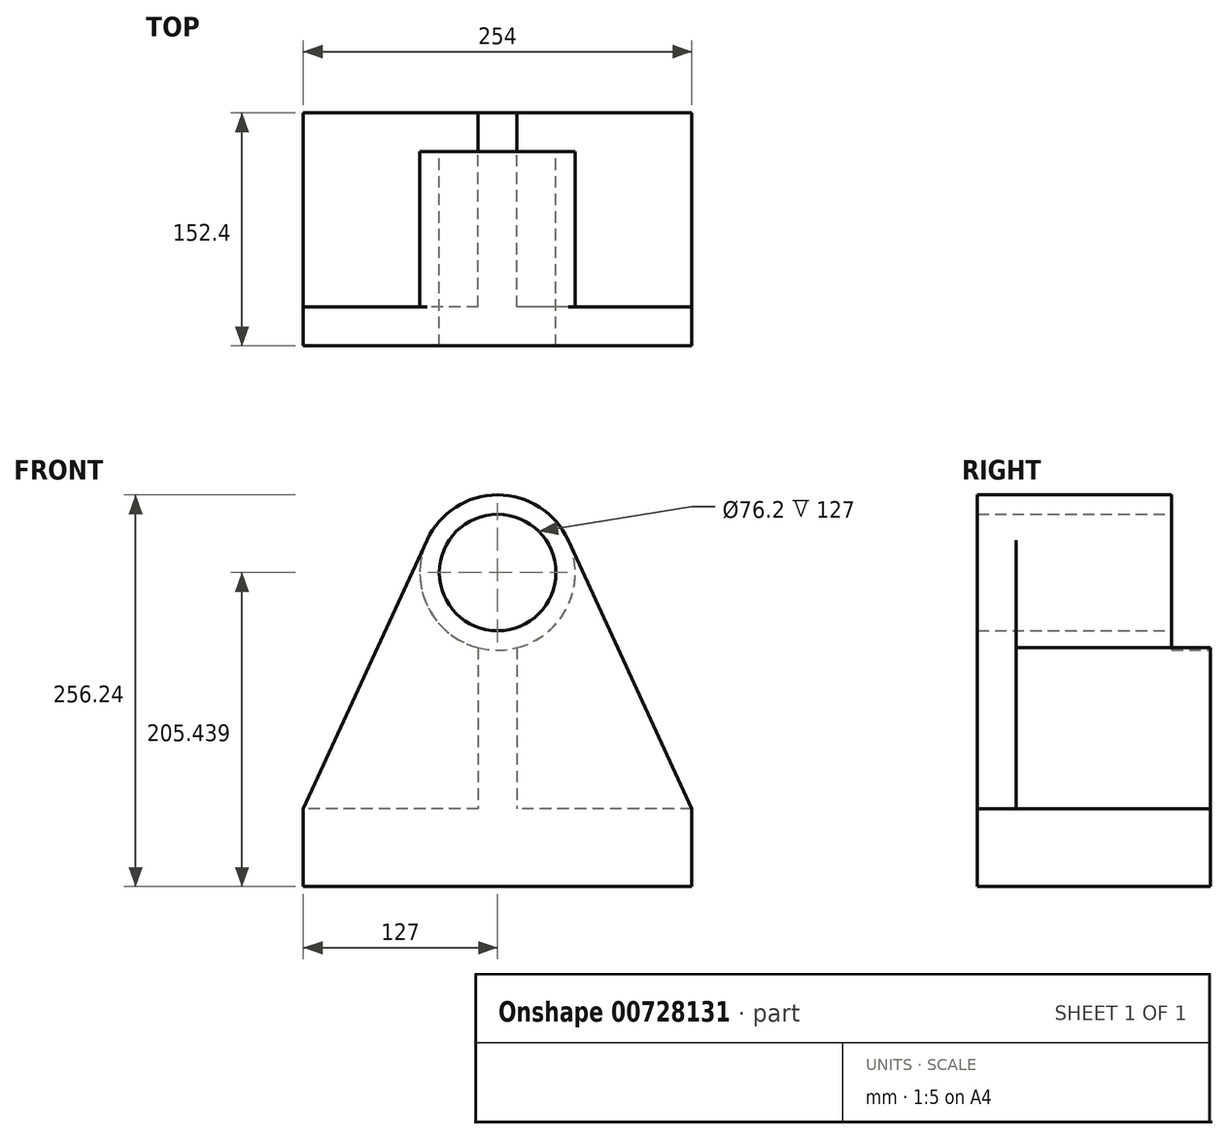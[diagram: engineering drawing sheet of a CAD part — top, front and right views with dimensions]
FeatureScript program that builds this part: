
annotation { "Feature Type Name" : "Feature", "Feature Type Description" : "" }
export const myFeature = defineFeature(function(context is Context, id is Id, definition is map)
    precondition{}
    {
        {
            var Q0;
            Q0=qCreatedBy(makeId("Front.planeOp"),FACE);
            var sketch = newSketch(context, id + "F0", { "sketchPlane" : qUnion([Q0])});
            skLineSegment(sketch, "E0", {"start": v(0, 0) * mm, "end": v(254, 0) * mm});
            skLineSegment(sketch, "E1", {"start": v(254, 0) * mm, "end": v(254, 50.8) * mm});
            skLineSegment(sketch, "E2", {"start": v(0, 0) * mm, "end": v(0, 50.8) * mm});
            skLineSegment(sketch, "E3", {"start": v(127, 0) * mm, "end": v(127, 205.44) * mm});
            skCircle(sketch, "E4", {"center": v(127, 205.44) * mm, "radius": 50.8 * mm});
            skLineSegment(sketch, "E5", {"start": v(254, 50.8) * mm, "end": v(173.16, 226.66) * mm});
            skLineSegment(sketch, "E6", {"start": v(0, 50.8) * mm, "end": v(80.84, 226.66) * mm});
            skSolve(sketch);
        }
        {
            var Q0;
            Q0 = qSketchRegion(id + "F0", true);
            extrude(context, id + "F1", {"entities" : qUnion([Q0]), "depth" : 152.4 * mm, "offsetDistance" : 25.4 * mm});
        }
        {
            var Q0;
            Q0=makeQuery(id+"F1.opExtrude","CAP_FACE",FACE,{"disambiguationData":[OSD([sQuery(id+"F0.wireOp",EDGE,"E0"),sQuery(id+"F0.wireOp",EDGE,"E1"),sQuery(id+"F0.wireOp",EDGE,"E2"),sQuery(id+"F0.wireOp",EDGE,"E4"),sQuery(id+"F0.wireOp",EDGE,"E5"),sQuery(id+"F0.wireOp",EDGE,"E6")])],"isStart":true});
            var sketch = newSketch(context, id + "F2", { "sketchPlane" : qUnion([Q0])});
            skCircle(sketch, "E7", {"center": v(-127, 205.44) * mm, "radius": 38.1 * mm});
            skSolve(sketch);
        }
        {
            var Q0;
            Q0=makeQuery(id+"F2.imprint","IMPRINT",FACE,{"disambiguationData":[TD([[makeQuery(id+"F2.imprint","IMPRINT",EDGE,{"derivedFrom":sQuery(id+"F2.wireOp",EDGE,"E7")}),1.0]])]});
            extrude(context, id + "F3", {"entities" : qUnion([Q0]), "operationType" : NewBodyOperationType.REMOVE, "oppositeDirection" : true, "depth" : 152.4 * mm, "offsetDistance" : 25.4 * mm});
        }
        {
            var Q0;
            Q0=makeQuery(id+"F1.opExtrude","CAP_FACE",FACE,{"disambiguationData":[OSD([sQuery(id+"F0.wireOp",EDGE,"E0"),sQuery(id+"F0.wireOp",EDGE,"E1"),sQuery(id+"F0.wireOp",EDGE,"E2"),sQuery(id+"F0.wireOp",EDGE,"E4"),sQuery(id+"F0.wireOp",EDGE,"E5"),sQuery(id+"F0.wireOp",EDGE,"E6")])],"isStart":true});
            var sketch = newSketch(context, id + "F4", { "sketchPlane" : qUnion([Q0])});
            skLineSegment(sketch, "E8", {"start": v(-254, 50.8) * mm, "end": v(0, 50.8) * mm});
            skLineSegment(sketch, "E9", {"start": v(0, 50.8) * mm, "end": v(-127, 50.8) * mm});
            skCircle(sketch, "E10", {"center": v(-127, 205.44) * mm, "radius": 50.8 * mm});
            skLineSegment(sketch, "E11", {"start": v(-114.3, 109.07) * mm, "end": v(-114.3, 156.25) * mm});
            skLineSegment(sketch, "E12", {"start": v(-114.3, 156.25) * mm, "end": v(-114.3, 50.8) * mm});
            skLineSegment(sketch, "E13", {"start": v(-139.7, 156.25) * mm, "end": v(-139.7, 50.8) * mm});
            skSolve(sketch);
        }
        {
            var Q0;
            {var subQ2=sQuery(id+"F4.wireOp",EDGE,"E13");Q0=makeQuery(id+"F4.imprint","IMPRINT",FACE,{"disambiguationData":[TD([[makeQuery(id+"F4.imprint","IMPRINT",EDGE,{"derivedFrom":subQ2}),-1.0]])]});}
            var Q1;
            {var subQ6=makeQuery(id+"F1.opExtrude","CAP_EDGE",EDGE,{"disambiguationData":[OSD([sQuery(id+"F0.wireOp",EDGE,"E6")])],"isStart":true});Q1=makeQuery(id+"F4.imprint","IMPRINT",FACE,{"disambiguationData":[TD([[makeQuery(id+"F4.imprint","IMPRINT",EDGE,{"derivedFrom":subQ6}),1.0]])]});}
            extrude(context, id + "F5", {"entities" : qUnion([Q0, Q1]), "operationType" : NewBodyOperationType.REMOVE, "oppositeDirection" : true, "depth" : 127 * mm, "offsetDistance" : 25.4 * mm});
        }
        {
            var Q0;
            Q0=makeQuery(id+"F1.opExtrude","CAP_FACE",FACE,{"disambiguationData":[OSD([sQuery(id+"F0.wireOp",EDGE,"E0"),sQuery(id+"F0.wireOp",EDGE,"E1"),sQuery(id+"F0.wireOp",EDGE,"E2"),sQuery(id+"F0.wireOp",EDGE,"E4"),sQuery(id+"F0.wireOp",EDGE,"E5"),sQuery(id+"F0.wireOp",EDGE,"E6")])],"isStart":true});
            var sketch = newSketch(context, id + "F6", { "sketchPlane" : qUnion([Q0])});
            skCircle(sketch, "E14", {"center": v(-127, 205.44) * mm, "radius": 50.8 * mm});
            skLineSegment(sketch, "E15", {"start": v(-139.7, 50.8) * mm, "end": v(-114.3, 50.8) * mm});
            skLineSegment(sketch, "E16", {"start": v(-114.3, 50.8) * mm, "end": v(-114.3, 156.25) * mm});
            skLineSegment(sketch, "E17", {"start": v(-139.7, 50.8) * mm, "end": v(-139.7, 156.25) * mm});
            skSolve(sketch);
        }
        {
            var Q0;
            Q0=makeQuery(id+"F6.imprint","IMPRINT",FACE,{"disambiguationData":[TD([[makeQuery(id+"F6.imprint","IMPRINT",EDGE,{"disambiguationData":[OD(0.0)],"derivedFrom":sQuery(id+"F6.wireOp",EDGE,"E14")}),-1.0]])]});
            extrude(context, id + "F7", {"entities" : qUnion([Q0]), "operationType" : NewBodyOperationType.REMOVE, "oppositeDirection" : true, "depth" : 25.4 * mm, "offsetDistance" : 25.4 * mm});
        }
    });
